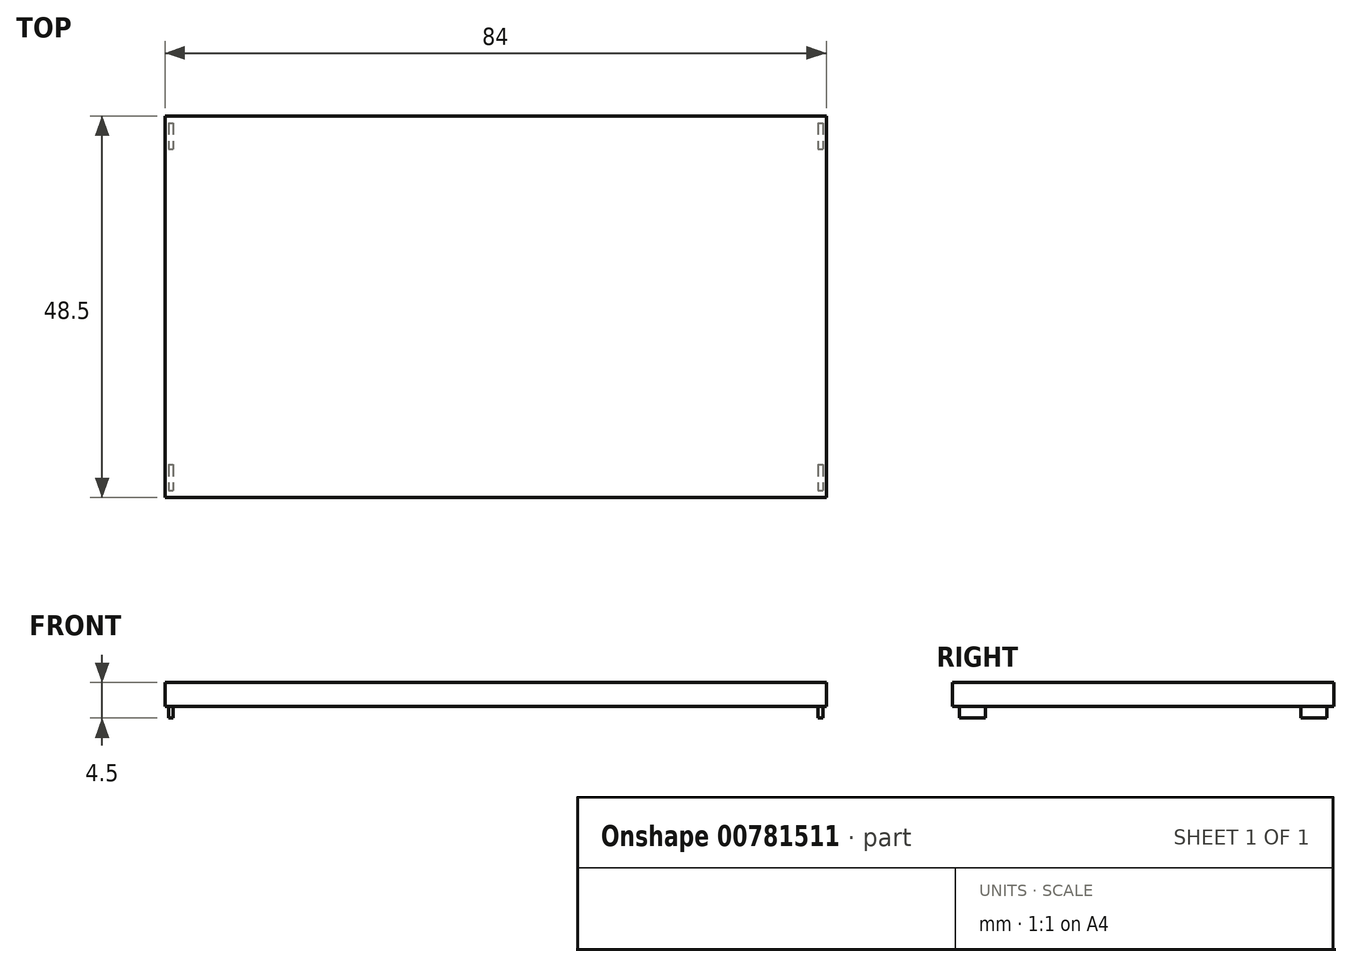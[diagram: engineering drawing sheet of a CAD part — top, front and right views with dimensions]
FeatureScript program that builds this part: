
annotation { "Feature Type Name" : "Feature", "Feature Type Description" : "" }
export const myFeature = defineFeature(function(context is Context, id is Id, definition is map)
    precondition{}
    {
        {
            var Q0;
            Q0=qCreatedBy(makeId("Top.planeOp"),FACE);
            var sketch = newSketch(context, id + "F0", { "sketchPlane" : qUnion([Q0])});
            skLineSegment(sketch, "E0.bottom", {"start": v(-40.55, -23.12) * mm, "end": v(-42.05, -23.12) * mm});
            skLineSegment(sketch, "E0.top", {"start": v(-40.55, 23.88) * mm, "end": v(-42.05, 23.88) * mm});
            skLineSegment(sketch, "E0.left", {"start": v(-40.55, -23.12) * mm, "end": v(-40.55, 23.88) * mm});
            skLineSegment(sketch, "E0.right", {"start": v(-42.05, -23.12) * mm, "end": v(-42.05, 23.88) * mm});
            skLineSegment(sketch, "E1.bottom", {"start": v(40.45, -23.12) * mm, "end": v(41.95, -23.12) * mm});
            skLineSegment(sketch, "E1.top", {"start": v(40.45, 23.88) * mm, "end": v(41.95, 23.88) * mm});
            skLineSegment(sketch, "E1.left", {"start": v(40.45, -23.12) * mm, "end": v(40.45, 23.88) * mm});
            skLineSegment(sketch, "E1.right", {"start": v(41.95, -23.12) * mm, "end": v(41.95, 23.88) * mm});
            skLineSegment(sketch, "E2.bottom", {"start": v(41.95, 23.88) * mm, "end": v(-42.05, 23.88) * mm});
            skLineSegment(sketch, "E2.top", {"start": v(41.95, 25.38) * mm, "end": v(-42.05, 25.38) * mm});
            skLineSegment(sketch, "E2.left", {"start": v(41.95, 23.88) * mm, "end": v(41.95, 25.38) * mm});
            skLineSegment(sketch, "E2.right", {"start": v(-42.05, 23.88) * mm, "end": v(-42.05, 25.38) * mm});
            skLineSegment(sketch, "E3.bottom", {"start": v(-40.55, -14.22) * mm, "end": v(-35.55, -14.22) * mm});
            skLineSegment(sketch, "E3.top", {"start": v(-40.55, -15.72) * mm, "end": v(-35.55, -15.72) * mm});
            skLineSegment(sketch, "E3.left", {"start": v(-40.55, -14.22) * mm, "end": v(-40.55, -15.72) * mm});
            skLineSegment(sketch, "E3.right", {"start": v(-35.55, -14.22) * mm, "end": v(-35.55, -15.72) * mm});
            skLineSegment(sketch, "E4.bottom", {"start": v(35.45, -15.72) * mm, "end": v(40.45, -15.72) * mm});
            skLineSegment(sketch, "E4.top", {"start": v(35.45, -14.22) * mm, "end": v(40.45, -14.22) * mm});
            skLineSegment(sketch, "E4.left", {"start": v(35.45, -15.72) * mm, "end": v(35.45, -14.22) * mm});
            skLineSegment(sketch, "E4.right", {"start": v(40.45, -15.72) * mm, "end": v(40.45, -14.22) * mm});
            skLineSegment(sketch, "E5.bottom", {"start": v(-41.7, -22.32) * mm, "end": v(-40.9, -22.32) * mm});
            skLineSegment(sketch, "E5.top", {"start": v(-41.7, -18.82) * mm, "end": v(-40.9, -18.82) * mm});
            skLineSegment(sketch, "E5.left", {"start": v(-41.7, -22.32) * mm, "end": v(-41.7, -18.82) * mm});
            skLineSegment(sketch, "E5.right", {"start": v(-40.9, -22.32) * mm, "end": v(-40.9, -18.82) * mm});
            skLineSegment(sketch, "E6.bottom", {"start": v(-41.7, 24.58) * mm, "end": v(-40.9, 24.58) * mm});
            skLineSegment(sketch, "E6.top", {"start": v(-41.7, 21.08) * mm, "end": v(-40.9, 21.08) * mm});
            skLineSegment(sketch, "E6.left", {"start": v(-41.7, 24.58) * mm, "end": v(-41.7, 21.08) * mm});
            skLineSegment(sketch, "E6.right", {"start": v(-40.9, 24.58) * mm, "end": v(-40.9, 21.08) * mm});
            skLineSegment(sketch, "E7.bottom", {"start": v(40.8, 24.58) * mm, "end": v(41.6, 24.58) * mm});
            skLineSegment(sketch, "E7.top", {"start": v(40.8, 21.08) * mm, "end": v(41.6, 21.08) * mm});
            skLineSegment(sketch, "E7.left", {"start": v(40.8, 24.58) * mm, "end": v(40.8, 21.08) * mm});
            skLineSegment(sketch, "E7.right", {"start": v(41.6, 24.58) * mm, "end": v(41.6, 21.08) * mm});
            skLineSegment(sketch, "E8.bottom", {"start": v(40.8, -18.82) * mm, "end": v(41.6, -18.82) * mm});
            skLineSegment(sketch, "E8.top", {"start": v(40.8, -22.32) * mm, "end": v(41.6, -22.32) * mm});
            skLineSegment(sketch, "E8.left", {"start": v(40.8, -18.82) * mm, "end": v(40.8, -22.32) * mm});
            skLineSegment(sketch, "E8.right", {"start": v(41.6, -18.82) * mm, "end": v(41.6, -22.32) * mm});
            skSolve(sketch);
        }
        {
            var Q0;
            Q0=qCreatedBy(makeId("Top.planeOp"),FACE);
            var sketch = newSketch(context, id + "F1", { "sketchPlane" : qUnion([Q0])});
            skLineSegment(sketch, "E9.bottom", {"start": v(-42.05, 25.38) * mm, "end": v(41.95, 25.38) * mm});
            skLineSegment(sketch, "E9.top", {"start": v(-42.05, -23.12) * mm, "end": v(41.95, -23.12) * mm});
            skLineSegment(sketch, "E9.left", {"start": v(-42.05, 25.38) * mm, "end": v(-42.05, -23.12) * mm});
            skLineSegment(sketch, "E9.right", {"start": v(41.95, 25.38) * mm, "end": v(41.95, -23.12) * mm});
            skLineSegment(sketch, "E10.bottom", {"start": v(-41.6, -18.92) * mm, "end": v(-41, -18.92) * mm});
            skLineSegment(sketch, "E10.top", {"start": v(-41.6, -22.22) * mm, "end": v(-41, -22.22) * mm});
            skLineSegment(sketch, "E10.left", {"start": v(-41.6, -18.92) * mm, "end": v(-41.6, -22.22) * mm});
            skLineSegment(sketch, "E10.right", {"start": v(-41, -18.92) * mm, "end": v(-41, -22.22) * mm});
            skLineSegment(sketch, "E11.bottom", {"start": v(-41.6, 24.48) * mm, "end": v(-41, 24.48) * mm});
            skLineSegment(sketch, "E11.top", {"start": v(-41.6, 21.18) * mm, "end": v(-41, 21.18) * mm});
            skLineSegment(sketch, "E11.left", {"start": v(-41.6, 24.48) * mm, "end": v(-41.6, 21.18) * mm});
            skLineSegment(sketch, "E11.right", {"start": v(-41, 24.48) * mm, "end": v(-41, 21.18) * mm});
            skLineSegment(sketch, "E12.bottom", {"start": v(40.9, 24.48) * mm, "end": v(41.5, 24.48) * mm});
            skLineSegment(sketch, "E12.top", {"start": v(40.9, 21.18) * mm, "end": v(41.5, 21.18) * mm});
            skLineSegment(sketch, "E12.left", {"start": v(40.9, 24.48) * mm, "end": v(40.9, 21.18) * mm});
            skLineSegment(sketch, "E12.right", {"start": v(41.5, 24.48) * mm, "end": v(41.5, 21.18) * mm});
            skLineSegment(sketch, "E13.bottom", {"start": v(40.9, -18.92) * mm, "end": v(41.5, -18.92) * mm});
            skLineSegment(sketch, "E13.top", {"start": v(40.9, -22.22) * mm, "end": v(41.5, -22.22) * mm});
            skLineSegment(sketch, "E13.left", {"start": v(40.9, -18.92) * mm, "end": v(40.9, -22.22) * mm});
            skLineSegment(sketch, "E13.right", {"start": v(41.5, -18.92) * mm, "end": v(41.5, -22.22) * mm});
            skSolve(sketch);
        }
        {
            var Q0;
            Q0 = qSketchRegion(id + "F1", true);
            var Q1;
            Q1=makeQuery(id+"F1.imprint","IMPRINT",FACE,{"disambiguationData":[TD([[makeQuery(id+"F1.imprint","IMPRINT",EDGE,{"derivedFrom":sQuery(id+"F1.wireOp",EDGE,"E13.bottom")}),-1.0]])]});
            var Q2;
            Q2=makeQuery(id+"F1.imprint","IMPRINT",FACE,{"disambiguationData":[TD([[makeQuery(id+"F1.imprint","IMPRINT",EDGE,{"derivedFrom":sQuery(id+"F1.wireOp",EDGE,"E12.bottom")}),-1.0]])]});
            var Q3;
            Q3=makeQuery(id+"F1.imprint","IMPRINT",FACE,{"disambiguationData":[TD([[makeQuery(id+"F1.imprint","IMPRINT",EDGE,{"derivedFrom":sQuery(id+"F1.wireOp",EDGE,"E10.bottom")}),-1.0]])]});
            var Q4;
            Q4=makeQuery(id+"F1.imprint","IMPRINT",FACE,{"disambiguationData":[TD([[makeQuery(id+"F1.imprint","IMPRINT",EDGE,{"derivedFrom":sQuery(id+"F1.wireOp",EDGE,"E11.bottom")}),-1.0]])]});
            extrude(context, id + "F2", {"entities" : qUnion([Q0, Q1, Q2, Q3, Q4]), "depth" : 3 * mm, "offsetDistance" : 25 * mm});
        }
        {
            var Q0;
            Q0=makeQuery(id+"F1.imprint","IMPRINT",FACE,{"disambiguationData":[TD([[makeQuery(id+"F1.imprint","IMPRINT",EDGE,{"derivedFrom":sQuery(id+"F1.wireOp",EDGE,"E10.bottom")}),-1.0]])]});
            var Q1;
            Q1=makeQuery(id+"F1.imprint","IMPRINT",FACE,{"disambiguationData":[TD([[makeQuery(id+"F1.imprint","IMPRINT",EDGE,{"derivedFrom":sQuery(id+"F1.wireOp",EDGE,"E11.bottom")}),-1.0]])]});
            var Q2;
            Q2=makeQuery(id+"F1.imprint","IMPRINT",FACE,{"disambiguationData":[TD([[makeQuery(id+"F1.imprint","IMPRINT",EDGE,{"derivedFrom":sQuery(id+"F1.wireOp",EDGE,"E13.bottom")}),-1.0]])]});
            var Q3;
            Q3=makeQuery(id+"F1.imprint","IMPRINT",FACE,{"disambiguationData":[TD([[makeQuery(id+"F1.imprint","IMPRINT",EDGE,{"derivedFrom":sQuery(id+"F1.wireOp",EDGE,"E12.bottom")}),-1.0]])]});
            extrude(context, id + "F3", {"entities" : qUnion([Q0, Q1, Q2, Q3]), "operationType" : NewBodyOperationType.ADD, "oppositeDirection" : true, "depth" : 1.5 * mm, "offsetDistance" : 25 * mm});
        }
    });
